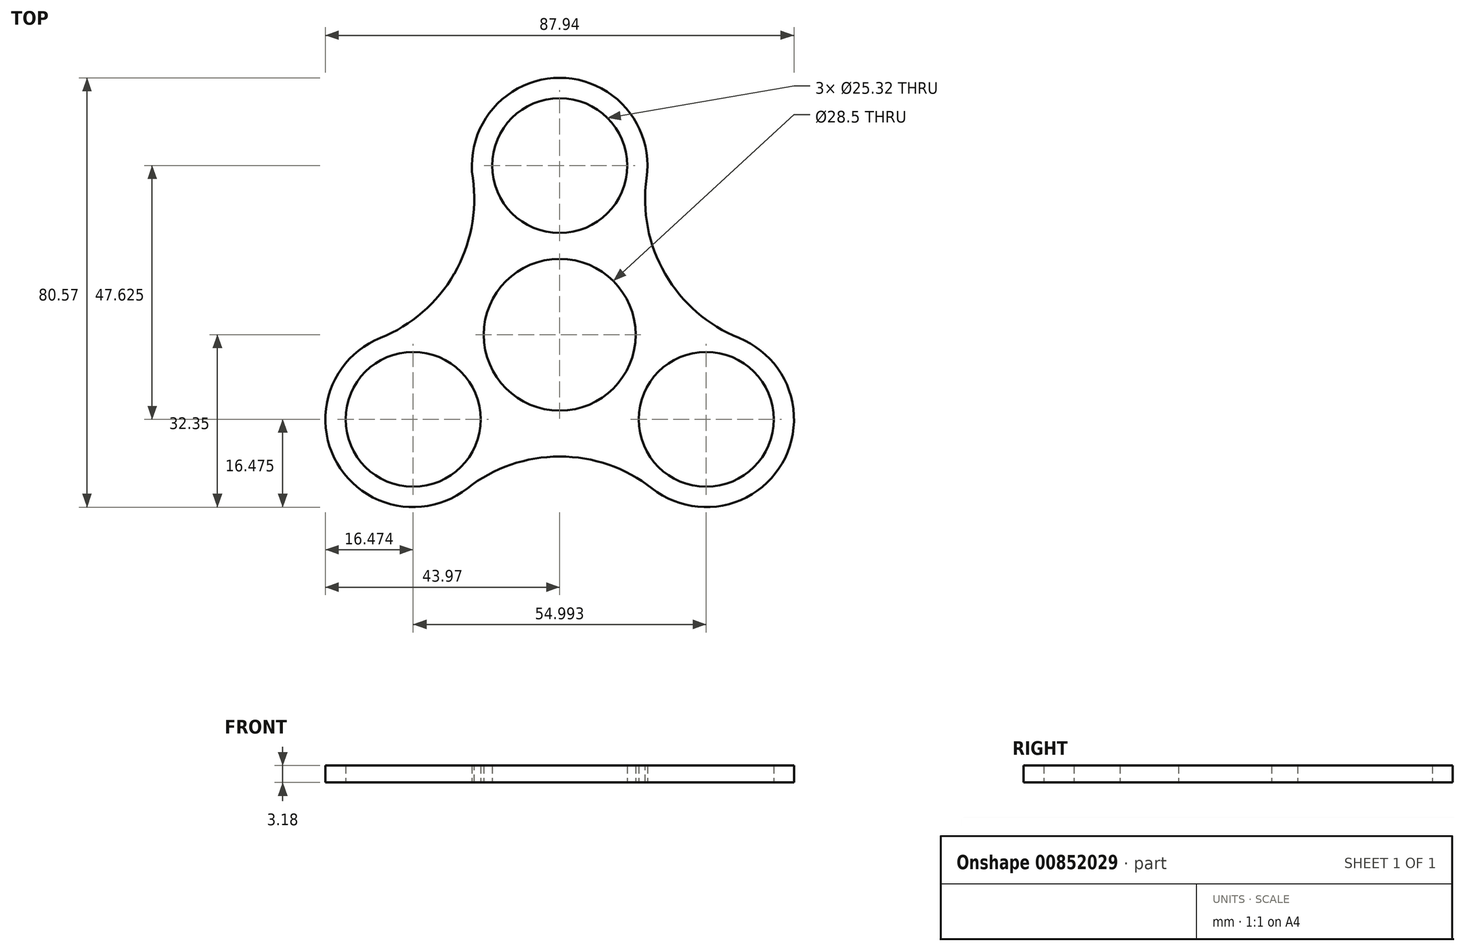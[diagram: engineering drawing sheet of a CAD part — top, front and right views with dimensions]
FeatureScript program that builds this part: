
annotation { "Feature Type Name" : "Feature", "Feature Type Description" : "" }
export const myFeature = defineFeature(function(context is Context, id is Id, definition is map)
    precondition{}
    {
        {
            var Q0;
            Q0=qCreatedBy(makeId("Top.planeOp"),FACE);
            var sketch = newSketch(context, id + "F0", { "sketchPlane" : qUnion([Q0])});
            skLineSegment(sketch, "E0", {"start": v(0, 0) * mm, "end": v(0, 31.75) * mm});
            skCircle(sketch, "E1", {"center": v(0, 31.75) * mm, "radius": 12.66 * mm});
            skCircle(sketch, "E2", {"center": v(0, 0) * mm, "radius": 14.25 * mm});
            skCircle(sketch, "E3", {"center": v(0, 31.75) * mm, "radius": 16.47 * mm});
            skCircle(sketch, "E4.1.0", {"center": v(-27.5, -15.87) * mm, "radius": 16.47 * mm});
            skCircle(sketch, "E4.1.1", {"center": v(-27.5, -15.87) * mm, "radius": 12.66 * mm});
            skCircle(sketch, "E4.2.0", {"center": v(27.5, -15.87) * mm, "radius": 16.47 * mm});
            skCircle(sketch, "E4.2.1", {"center": v(27.5, -15.87) * mm, "radius": 12.66 * mm});
            skCircle(sketch, "E5", {"center": v(0, 0) * mm, "radius": 22.86 * mm});
            skSolve(sketch);
        }
        {
            var Q0;
            Q0 = qSketchRegion(id + "F0", true);
            extrude(context, id + "F1", {"entities" : qUnion([Q0]), "depth" : 3.17 * mm, "offsetDistance" : 25.4 * mm});
        }
        {
            var Q0;
            {var subQ0=sQuery(id+"F0.wireOp",EDGE,"E5");var subQ1=sQuery(id+"F0.wireOp",EDGE,"E3");Q0=makeQuery(id+"F1.opExtrude","SWEPT_EDGE",EDGE,{"disambiguationData":[OSD([subQ1,subQ0]),TDD([makeQuery(id+"F0.imprint","INTERSECT",VERTEX,{"disambiguationData":[OD(0.0)],"derivedFrom":[subQ1,subQ0]})])]});}
            var Q1;
            {var subQ0=sQuery(id+"F0.wireOp",EDGE,"E5");var subQ1=sQuery(id+"F0.wireOp",EDGE,"E4.1.0");Q1=makeQuery(id+"F1.opExtrude","SWEPT_EDGE",EDGE,{"disambiguationData":[OSD([subQ1,subQ0]),TDD([makeQuery(id+"F0.imprint","INTERSECT",VERTEX,{"disambiguationData":[OD(0.0)],"derivedFrom":[subQ1,subQ0]})])]});}
            var Q2;
            {var subQ0=sQuery(id+"F0.wireOp",EDGE,"E5");var subQ1=sQuery(id+"F0.wireOp",EDGE,"E4.1.0");Q2=makeQuery(id+"F1.opExtrude","SWEPT_EDGE",EDGE,{"disambiguationData":[OSD([subQ1,subQ0]),TDD([makeQuery(id+"F0.imprint","INTERSECT",VERTEX,{"disambiguationData":[OD(1.0)],"derivedFrom":[subQ1,subQ0]})])]});}
            var Q3;
            {var subQ0=sQuery(id+"F0.wireOp",EDGE,"E5");var subQ1=sQuery(id+"F0.wireOp",EDGE,"E4.2.0");Q3=makeQuery(id+"F1.opExtrude","SWEPT_EDGE",EDGE,{"disambiguationData":[OSD([subQ1,subQ0]),TDD([makeQuery(id+"F0.imprint","INTERSECT",VERTEX,{"disambiguationData":[OD(0.0)],"derivedFrom":[subQ1,subQ0]})])]});}
            var Q4;
            {var subQ0=sQuery(id+"F0.wireOp",EDGE,"E5");var subQ1=sQuery(id+"F0.wireOp",EDGE,"E4.2.0");Q4=makeQuery(id+"F1.opExtrude","SWEPT_EDGE",EDGE,{"disambiguationData":[OSD([subQ1,subQ0]),TDD([makeQuery(id+"F0.imprint","INTERSECT",VERTEX,{"disambiguationData":[OD(1.0)],"derivedFrom":[subQ1,subQ0]})])]});}
            var Q5;
            {var subQ0=sQuery(id+"F0.wireOp",EDGE,"E5");var subQ1=sQuery(id+"F0.wireOp",EDGE,"E3");Q5=makeQuery(id+"F1.opExtrude","SWEPT_EDGE",EDGE,{"disambiguationData":[OSD([subQ1,subQ0]),TDD([makeQuery(id+"F0.imprint","INTERSECT",VERTEX,{"disambiguationData":[OD(1.0)],"derivedFrom":[subQ1,subQ0]})])]});}
            fillet(context, id + "F2", {"entities" : qUnion([Q0, Q1, Q2, Q3, Q4, Q5]), "radius" : 27.94 * mm, "tangentPropagation" : true, "allowEdgeOverflow" : false});
        }
    });
